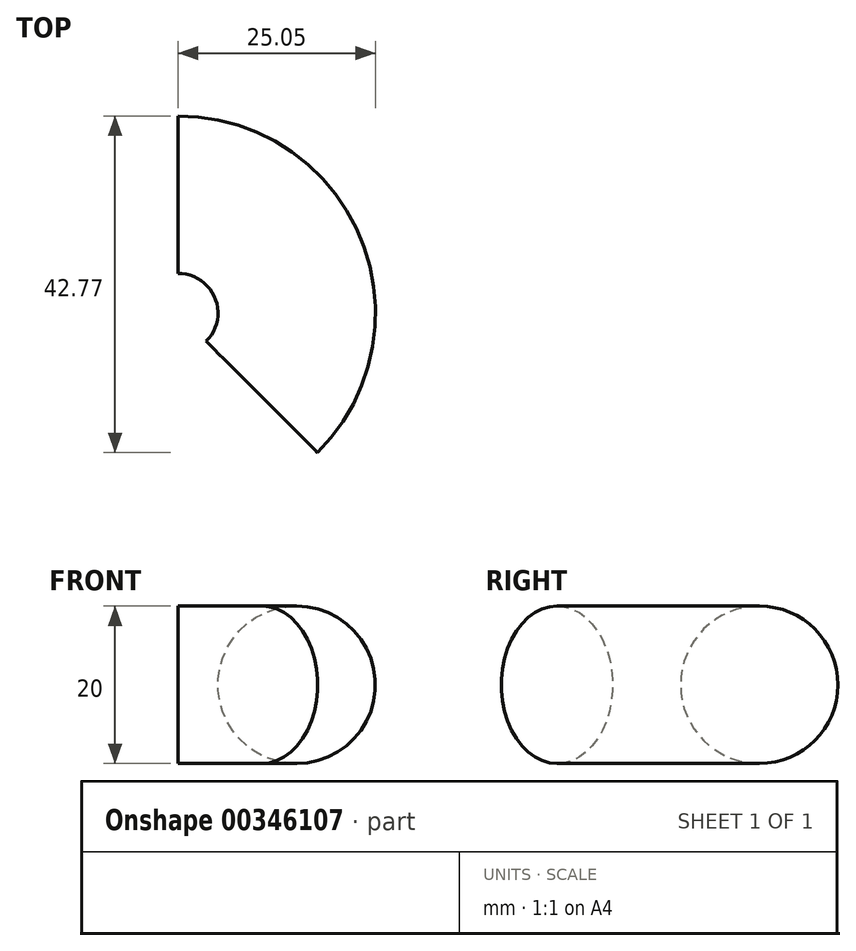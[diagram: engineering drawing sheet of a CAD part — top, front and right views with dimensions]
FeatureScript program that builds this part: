
annotation { "Feature Type Name" : "Feature", "Feature Type Description" : "" }
export const myFeature = defineFeature(function(context is Context, id is Id, definition is map)
    precondition{}
    {
        {
            var Q0;
            Q0=qCreatedBy(makeId("Front.planeOp"),FACE);
            var sketch = newSketch(context, id + "F0", { "sketchPlane" : qUnion([Q0])});
            skCircle(sketch, "E0", {"center": v(0, 0) * mm, "radius": 10 * mm});
            skSolve(sketch);
        }
        {
            var Q0;
            Q0=qCreatedBy(makeId("Front.planeOp"),FACE);
            var sketch = newSketch(context, id + "F1", { "sketchPlane" : qUnion([Q0])});
            skLineSegment(sketch, "E1", {"start": v(-15.05, 9.83) * mm, "end": v(-15.05, -8.09) * mm});
            skSolve(sketch);
        }
        {
            var Q0;
            Q0=makeQuery(id+"F0.imprint","IMPRINT",FACE,{"disambiguationData":[TD([[makeQuery(id+"F0.imprint","IMPRINT",EDGE,{"derivedFrom":sQuery(id+"F0.wireOp",EDGE,"E0")}),1.0]])]});
            var Q1;
            Q1=sQuery(id+"F1.wireOp",EDGE,"E1");
            revolve(context, id + "F2", {"entities" : qUnion([Q0]), "axis" : qUnion([Q1]), "revolveType" : RevolveType.TWO_DIRECTIONS, "angle" : 45 * degree, "angleBack" : 270 * degree});
        }
    });
